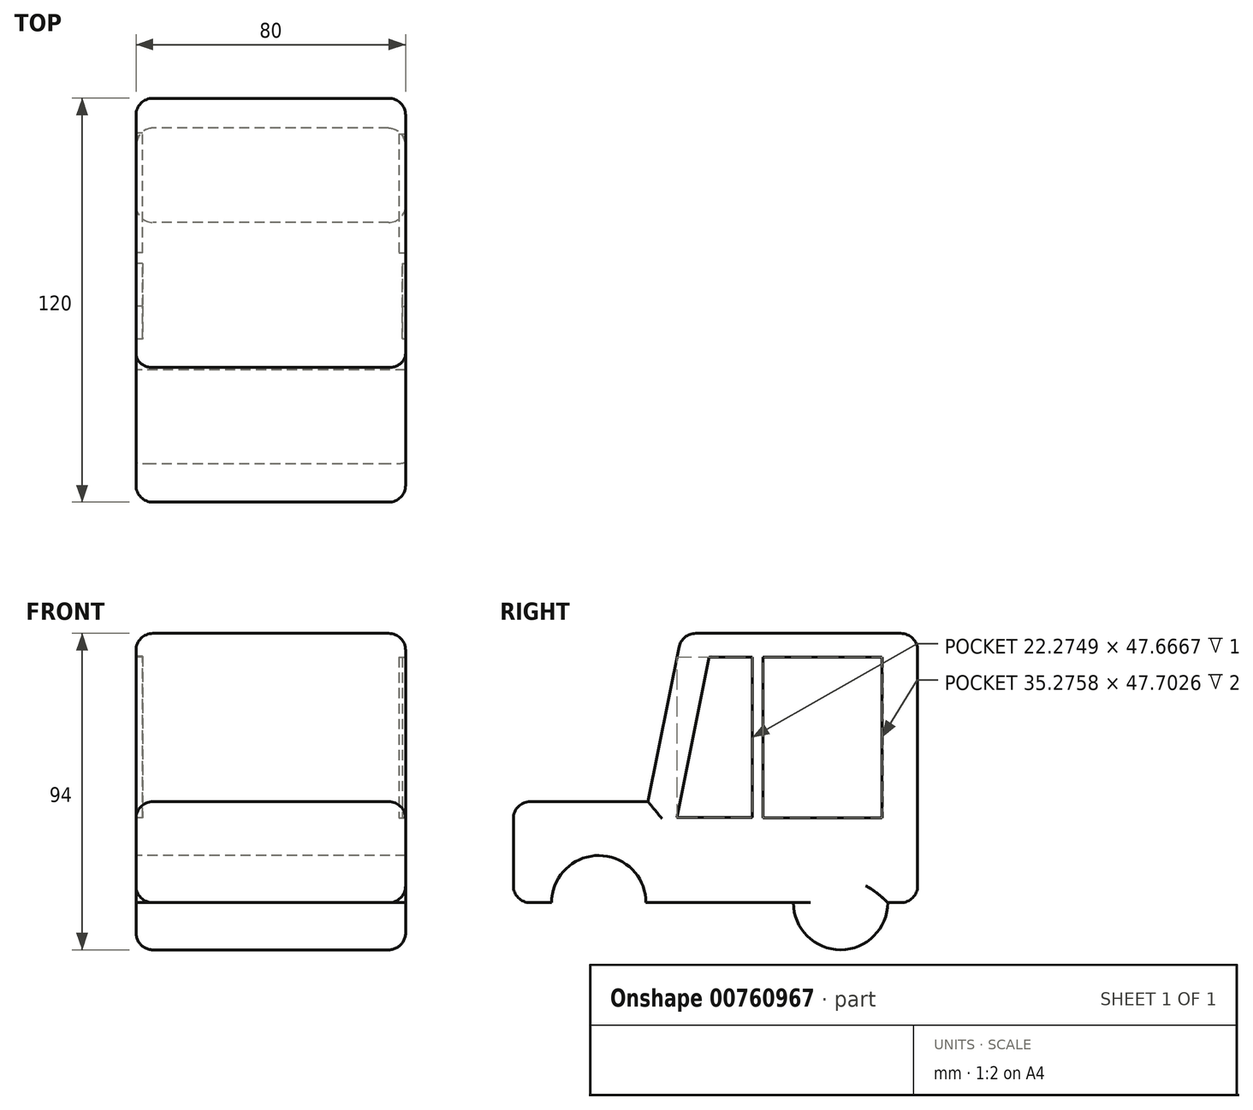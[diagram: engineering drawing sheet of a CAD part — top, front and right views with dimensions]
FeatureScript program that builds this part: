
annotation { "Feature Type Name" : "Feature", "Feature Type Description" : "" }
export const myFeature = defineFeature(function(context is Context, id is Id, definition is map)
    precondition{}
    {
        {
            var Q0;
            Q0=qCreatedBy(makeId("Right.planeOp"),FACE);
            var sketch = newSketch(context, id + "F0", { "sketchPlane" : qUnion([Q0])});
            skLineSegment(sketch, "E0", {"start": v(61.85, 80) * mm, "end": v(-8.15, 80) * mm});
            skLineSegment(sketch, "E1", {"start": v(-8.15, 80) * mm, "end": v(-18.15, 30) * mm});
            skLineSegment(sketch, "E2", {"start": v(-18.15, 30) * mm, "end": v(-58.15, 30) * mm});
            skLineSegment(sketch, "E3", {"start": v(-58.15, 30) * mm, "end": v(-58.15, 0) * mm});
            skLineSegment(sketch, "E4", {"start": v(-58.15, 0) * mm, "end": v(61.85, 0) * mm});
            skLineSegment(sketch, "E5", {"start": v(61.85, 0) * mm, "end": v(61.85, 80) * mm});
            skCircle(sketch, "E6", {"center": v(-32.81, 0) * mm, "radius": 14 * mm});
            skCircle(sketch, "E7", {"center": v(38.99, 0) * mm, "radius": 14 * mm});
            skSolve(sketch);
        }
        {
            var Q0;
            Q0=makeQuery(id+"F0.imprint","IMPRINT",FACE,{"disambiguationData":[TD([[makeQuery(id+"F0.imprint","IMPRINT",EDGE,{"derivedFrom":sQuery(id+"F0.wireOp",EDGE,"E0")}),1.0]])]});
            var sketch = newSketch(context, id + "F1", { "sketchPlane" : qUnion([Q0])});
            skSolve(sketch);
        }
        {
            var Q0;
            Q0 = qSketchRegion(id + "F1", true);
            var Q1;
            Q1=makeQuery(id+"F0.imprint","IMPRINT",FACE,{"disambiguationData":[TD([[makeQuery(id+"F0.imprint","IMPRINT",EDGE,{"derivedFrom":sQuery(id+"F0.wireOp",EDGE,"E0")}),1.0]])]});
            extrude(context, id + "F2", {"entities" : qUnion([Q0, Q1]), "depth" : 80 * mm, "offsetDistance" : 25 * mm});
        }
        {
            var Q0;
            {var subQ0=sQuery(id+"F0.wireOp",EDGE,"E6");var subQ1=sQuery(id+"F0.wireOp",EDGE,"E4");var subQ2=makeQuery(id+"F0.imprint","INTERSECT",VERTEX,{"disambiguationData":[OD(0.0)],"derivedFrom":[subQ1,subQ0]});Q0=makeQuery(id+"F0.imprint","IMPRINT",FACE,{"disambiguationData":[TD([[makeQuery(id+"F0.imprint","IMPRINT",EDGE,{"disambiguationData":[TD([[subQ2,-1.0]])],"derivedFrom":subQ1}),-1.0]])]});}
            var Q1;
            {var subQ0=sQuery(id+"F0.wireOp",EDGE,"E6");var subQ1=sQuery(id+"F0.wireOp",EDGE,"E4");var subQ2=makeQuery(id+"F0.imprint","INTERSECT",VERTEX,{"disambiguationData":[OD(0.0)],"derivedFrom":[subQ1,subQ0]});Q1=makeQuery(id+"F0.imprint","IMPRINT",FACE,{"disambiguationData":[TD([[makeQuery(id+"F0.imprint","IMPRINT",EDGE,{"disambiguationData":[TD([[subQ2,-1.0]])],"derivedFrom":subQ1}),1.0]])]});}
            extrude(context, id + "F3", {"entities" : qUnion([Q0, Q1]), "operationType" : NewBodyOperationType.ADD, "depth" : 80 * mm, "offsetDistance" : 25 * mm});
        }
        {
            var Q0;
            {var subQ0=sQuery(id+"F0.wireOp",EDGE,"E7");var subQ1=sQuery(id+"F0.wireOp",EDGE,"E4");var subQ2=makeQuery(id+"F0.imprint","INTERSECT",VERTEX,{"disambiguationData":[OD(0.0)],"derivedFrom":[subQ1,subQ0]});Q0=makeQuery(id+"F0.imprint","IMPRINT",FACE,{"disambiguationData":[TD([[makeQuery(id+"F0.imprint","IMPRINT",EDGE,{"disambiguationData":[TD([[subQ2,-1.0]])],"derivedFrom":subQ1}),1.0]])]});}
            var Q1;
            {var subQ0=sQuery(id+"F0.wireOp",EDGE,"E7");var subQ1=sQuery(id+"F0.wireOp",EDGE,"E4");var subQ2=makeQuery(id+"F0.imprint","INTERSECT",VERTEX,{"disambiguationData":[OD(0.0)],"derivedFrom":[subQ1,subQ0]});Q1=makeQuery(id+"F0.imprint","IMPRINT",FACE,{"disambiguationData":[TD([[makeQuery(id+"F0.imprint","IMPRINT",EDGE,{"disambiguationData":[TD([[subQ2,-1.0]])],"derivedFrom":subQ1}),-1.0]])]});}
            extrude(context, id + "F4", {"entities" : qUnion([Q0, Q1]), "operationType" : NewBodyOperationType.ADD, "depth" : 80 * mm, "offsetDistance" : 25 * mm});
        }
        {
            var Q0;
            Q0=makeQuery(id+"F2.opExtrude","CAP_EDGE",EDGE,{"disambiguationData":[OSD([sQuery(id+"F0.wireOp",EDGE,"E1")])],"isStart":false});
            var Q1;
            Q1=makeQuery(id+"F2.opExtrude","CAP_EDGE",EDGE,{"disambiguationData":[OSD([sQuery(id+"F0.wireOp",EDGE,"E0")])],"isStart":false});
            var Q2;
            Q2=makeQuery(id+"F2.opExtrude","SWEPT_EDGE",EDGE,{"disambiguationData":[OSD([sQuery(id+"F0.wireOp",EDGE,"E0"),sQuery(id+"F0.wireOp",EDGE,"E1")])]});
            var Q3;
            Q3=makeQuery(id+"F2.opExtrude","CAP_EDGE",EDGE,{"disambiguationData":[OSD([sQuery(id+"F0.wireOp",EDGE,"E2")])],"isStart":false});
            var Q4;
            Q4=makeQuery(id+"F2.opExtrude","SWEPT_EDGE",EDGE,{"disambiguationData":[OSD([sQuery(id+"F0.wireOp",EDGE,"E2"),sQuery(id+"F0.wireOp",EDGE,"E3")])]});
            var Q5;
            Q5=makeQuery(id+"F2.opExtrude","CAP_EDGE",EDGE,{"disambiguationData":[OSD([sQuery(id+"F0.wireOp",EDGE,"E3")])],"isStart":false});
            var Q6;
            Q6=makeQuery(id+"F2.opExtrude","CAP_EDGE",EDGE,{"disambiguationData":[OSD([sQuery(id+"F0.wireOp",EDGE,"E3")])],"isStart":true});
            var Q7;
            Q7=makeQuery(id+"F2.opExtrude","SWEPT_EDGE",EDGE,{"disambiguationData":[OSD([sQuery(id+"F0.wireOp",EDGE,"E3"),sQuery(id+"F0.wireOp",EDGE,"E4")])]});
            var Q8;
            Q8=makeQuery(id+"F3.opExtrude","CAP_EDGE",EDGE,{"disambiguationData":[OSD([sQuery(id+"F0.wireOp",EDGE,"E6")])],"isStart":true});
            var Q9;
            Q9=makeQuery(id+"F3.opExtrude","CAP_EDGE",EDGE,{"disambiguationData":[OSD([sQuery(id+"F0.wireOp",EDGE,"E6")])],"isStart":false});
            var Q10;
            Q10=makeQuery(id+"F4.opExtrude","CAP_EDGE",EDGE,{"disambiguationData":[OSD([sQuery(id+"F0.wireOp",EDGE,"E7")])],"isStart":false});
            var Q11;
            Q11=makeQuery(id+"F4.opExtrude","CAP_EDGE",EDGE,{"disambiguationData":[OSD([sQuery(id+"F0.wireOp",EDGE,"E7")])],"isStart":true});
            var Q12;
            Q12=makeQuery(id+"F2.opExtrude","CAP_EDGE",EDGE,{"disambiguationData":[OSD([sQuery(id+"F0.wireOp",EDGE,"E5")])],"isStart":false});
            var Q13;
            Q13=makeQuery(id+"F2.opExtrude","CAP_EDGE",EDGE,{"disambiguationData":[OSD([sQuery(id+"F0.wireOp",EDGE,"E5")])],"isStart":true});
            var Q14;
            Q14=makeQuery(id+"F2.opExtrude","CAP_EDGE",EDGE,{"disambiguationData":[OSD([sQuery(id+"F0.wireOp",EDGE,"E0")])],"isStart":true});
            var Q15;
            Q15=makeQuery(id+"F2.opExtrude","SWEPT_EDGE",EDGE,{"disambiguationData":[OSD([sQuery(id+"F0.wireOp",EDGE,"E0"),sQuery(id+"F0.wireOp",EDGE,"E5")])]});
            var Q16;
            {var subQ0=sQuery(id+"F0.wireOp",EDGE,"E4");Q16=makeQuery(id+"F2.opExtrude","CAP_EDGE",EDGE,{"disambiguationData":[OSD([subQ0]),TDD([makeQuery(id+"F0.imprint","IMPRINT",EDGE,{"disambiguationData":[TD([[makeQuery(id+"F0.imprint","INTERSECT",VERTEX,{"disambiguationData":[OD(1.0)],"derivedFrom":[subQ0,sQuery(id+"F0.wireOp",EDGE,"E6")]}),-1.0]])],"derivedFrom":subQ0})])],"isStart":true});}
            var Q17;
            {var subQ0=sQuery(id+"F0.wireOp",EDGE,"E4");Q17=makeQuery(id+"F2.opExtrude","CAP_EDGE",EDGE,{"disambiguationData":[OSD([subQ0]),TDD([makeQuery(id+"F0.imprint","IMPRINT",EDGE,{"disambiguationData":[TD([[makeQuery(id+"F0.imprint","INTERSECT",VERTEX,{"disambiguationData":[OD(1.0)],"derivedFrom":[subQ0,sQuery(id+"F0.wireOp",EDGE,"E6")]}),-1.0]])],"derivedFrom":subQ0})])],"isStart":false});}
            fillet(context, id + "F5", {"entities" : qUnion([Q0, Q1, Q2, Q3, Q4, Q5, Q6, Q7, Q8, Q9, Q10, Q11, Q12, Q13, Q14, Q15, Q16, Q17]), "radius" : 5 * mm, "tangentPropagation" : true, "allowEdgeOverflow" : false});
        }
        {
            var Q0;
            Q0=makeQuery(id+"F2.opExtrude","CAP_EDGE",EDGE,{"disambiguationData":[OSD([sQuery(id+"F0.wireOp",EDGE,"E2")])],"isStart":true});
            fillet(context, id + "F6", {"entities" : qUnion([Q0]), "radius" : 5 * mm, "tangentPropagation" : true, "allowEdgeOverflow" : false});
        }
        {
            var Q0;
            {var subQ0=sQuery(id+"F0.wireOp",EDGE,"E4");Q0=makeQuery(id+"F2.opExtrude","CAP_EDGE",EDGE,{"disambiguationData":[OSD([subQ0]),TDD([makeQuery(id+"F0.imprint","IMPRINT",EDGE,{"disambiguationData":[TD([[makeQuery(id+"F0.imprint","INTERSECT",VERTEX,{"derivedFrom":[sQuery(id+"F0.wireOp",EDGE,"E3"),subQ0]}),-1.0]])],"derivedFrom":subQ0})])],"isStart":false});}
            var Q1;
            {var subQ0=sQuery(id+"F0.wireOp",EDGE,"E4");Q1=makeQuery(id+"F2.opExtrude","CAP_EDGE",EDGE,{"disambiguationData":[OSD([subQ0]),TDD([makeQuery(id+"F0.imprint","IMPRINT",EDGE,{"disambiguationData":[TD([[makeQuery(id+"F0.imprint","INTERSECT",VERTEX,{"derivedFrom":[sQuery(id+"F0.wireOp",EDGE,"E3"),subQ0]}),-1.0]])],"derivedFrom":subQ0})])],"isStart":true});}
            fillet(context, id + "F7", {"entities" : qUnion([Q0, Q1]), "radius" : 5 * mm, "tangentPropagation" : true, "allowEdgeOverflow" : false});
        }
        {
            var Q0;
            {var subQ0=sQuery(id+"F0.wireOp",EDGE,"E7");var subQ1=sQuery(id+"F0.wireOp",EDGE,"E6");Q0=makeQuery(id+"F4.boolean.opBoolean","MERGE",FACE,{"derivedFrom":[makeQuery(id+"F3.boolean.opBoolean","MERGE",FACE,{"derivedFrom":[makeQuery(id+"F2.opExtrude","CAP_FACE",FACE,{"disambiguationData":[OSD([sQuery(id+"F0.wireOp",EDGE,"E0"),sQuery(id+"F0.wireOp",EDGE,"E1"),sQuery(id+"F0.wireOp",EDGE,"E2"),sQuery(id+"F0.wireOp",EDGE,"E3"),sQuery(id+"F0.wireOp",EDGE,"E4"),sQuery(id+"F0.wireOp",EDGE,"E5"),subQ1,subQ0])],"isStart":false}),makeQuery(id+"F3.opExtrude","CAP_FACE",FACE,{"disambiguationData":[OSD([subQ1])],"isStart":false})]}),makeQuery(id+"F4.opExtrude","CAP_FACE",FACE,{"disambiguationData":[OSD([subQ0])],"isStart":false})]});}
            var sketch = newSketch(context, id + "F8", { "sketchPlane" : qUnion([Q0])});
            skLineSegment(sketch, "E8", {"start": v(0, 72.95) * mm, "end": v(-9.53, 25.28) * mm});
            skLineSegment(sketch, "E9", {"start": v(-9.53, 25.28) * mm, "end": v(12.74, 25.28) * mm});
            skLineSegment(sketch, "E10", {"start": v(12.74, 25.28) * mm, "end": v(12.74, 72.95) * mm});
            skLineSegment(sketch, "E11", {"start": v(12.74, 72.95) * mm, "end": v(0, 72.95) * mm});
            skSolve(sketch);
        }
        {
            var Q0;
            Q0 = qSketchRegion(id + "F8", true);
            extrude(context, id + "F9", {"entities" : qUnion([Q0]), "operationType" : NewBodyOperationType.REMOVE, "endBound" : BoundingType.SYMMETRIC, "oppositeDirection" : true, "depth" : 2 * mm, "offsetDistance" : 25 * mm});
        }
        {
            var Q0;
            Q0=makeQuery(id+"F0.imprint","IMPRINT",FACE,{"disambiguationData":[TD([[makeQuery(id+"F0.imprint","IMPRINT",EDGE,{"derivedFrom":sQuery(id+"F0.wireOp",EDGE,"E0")}),1.0]])]});
            var sketch = newSketch(context, id + "F10", { "sketchPlane" : qUnion([Q0])});
            skLineSegment(sketch, "E12", {"start": v(0, 73.15) * mm, "end": v(-9.72, 25.25) * mm});
            skLineSegment(sketch, "E13", {"start": v(-9.72, 25.25) * mm, "end": v(12.73, 25.25) * mm});
            skLineSegment(sketch, "E14", {"start": v(12.73, 25.25) * mm, "end": v(12.73, 72.95) * mm});
            skLineSegment(sketch, "E15", {"start": v(12.73, 72.95) * mm, "end": v(0, 73.15) * mm});
            skSolve(sketch);
        }
        {
            var Q0;
            Q0 = qSketchRegion(id + "F10", true);
            extrude(context, id + "F11", {"entities" : qUnion([Q0]), "operationType" : NewBodyOperationType.REMOVE, "depth" : 2 * mm, "offsetDistance" : 25 * mm});
        }
        {
            var Q0;
            Q0=makeQuery(id+"F2.opExtrude","CAP_EDGE",EDGE,{"disambiguationData":[OSD([sQuery(id+"F0.wireOp",EDGE,"E1")])],"isStart":true});
            fillet(context, id + "F12", {"entities" : qUnion([Q0]), "radius" : 5 * mm, "tangentPropagation" : true, "allowEdgeOverflow" : false});
        }
        {
            var Q0;
            Q0=makeQuery(id+"F0.imprint","IMPRINT",FACE,{"disambiguationData":[TD([[makeQuery(id+"F0.imprint","IMPRINT",EDGE,{"derivedFrom":sQuery(id+"F0.wireOp",EDGE,"E0")}),1.0]])]});
            var sketch = newSketch(context, id + "F13", { "sketchPlane" : qUnion([Q0])});
            skLineSegment(sketch, "E16", {"start": v(15.93, 72.95) * mm, "end": v(51.51, 72.95) * mm});
            skLineSegment(sketch, "E17", {"start": v(51.51, 72.95) * mm, "end": v(51.51, 25.25) * mm});
            skLineSegment(sketch, "E18", {"start": v(51.51, 25.25) * mm, "end": v(15.93, 25.25) * mm});
            skLineSegment(sketch, "E19", {"start": v(15.93, 25.25) * mm, "end": v(15.93, 72.95) * mm});
            skSolve(sketch);
        }
        {
            var Q0;
            Q0 = qSketchRegion(id + "F13", true);
            extrude(context, id + "F14", {"entities" : qUnion([Q0]), "operationType" : NewBodyOperationType.REMOVE, "depth" : 2 * mm, "offsetDistance" : 25 * mm});
        }
        {
            var Q0;
            {var subQ0=sQuery(id+"F0.wireOp",EDGE,"E7");var subQ1=sQuery(id+"F0.wireOp",EDGE,"E6");Q0=makeQuery(id+"F4.boolean.opBoolean","MERGE",FACE,{"derivedFrom":[makeQuery(id+"F3.boolean.opBoolean","MERGE",FACE,{"derivedFrom":[makeQuery(id+"F2.opExtrude","CAP_FACE",FACE,{"disambiguationData":[OSD([sQuery(id+"F0.wireOp",EDGE,"E0"),sQuery(id+"F0.wireOp",EDGE,"E1"),sQuery(id+"F0.wireOp",EDGE,"E2"),sQuery(id+"F0.wireOp",EDGE,"E3"),sQuery(id+"F0.wireOp",EDGE,"E4"),sQuery(id+"F0.wireOp",EDGE,"E5"),subQ1,subQ0])],"isStart":false}),makeQuery(id+"F3.opExtrude","CAP_FACE",FACE,{"disambiguationData":[OSD([subQ1])],"isStart":false})]}),makeQuery(id+"F4.opExtrude","CAP_FACE",FACE,{"disambiguationData":[OSD([subQ0])],"isStart":false})]});}
            var sketch = newSketch(context, id + "F15", { "sketchPlane" : qUnion([Q0])});
            skLineSegment(sketch, "E20", {"start": v(15.93, 72.95) * mm, "end": v(15.93, 25.25) * mm});
            skLineSegment(sketch, "E21", {"start": v(15.93, 25.25) * mm, "end": v(51.21, 25.25) * mm});
            skLineSegment(sketch, "E22", {"start": v(51.21, 25.25) * mm, "end": v(51.21, 72.95) * mm});
            skLineSegment(sketch, "E23", {"start": v(51.21, 72.95) * mm, "end": v(15.93, 72.95) * mm});
            skSolve(sketch);
        }
        {
            var Q0;
            Q0 = qSketchRegion(id + "F15", true);
            extrude(context, id + "F16", {"entities" : qUnion([Q0]), "operationType" : NewBodyOperationType.REMOVE, "oppositeDirection" : true, "depth" : 2 * mm, "offsetDistance" : 25 * mm});
        }
        {
            var Q0;
            Q0=makeQuery(id+"F2.opExtrude","SWEPT_EDGE",EDGE,{"disambiguationData":[OSD([sQuery(id+"F0.wireOp",EDGE,"E4"),sQuery(id+"F0.wireOp",EDGE,"E5")])]});
            fillet(context, id + "F17", {"entities" : qUnion([Q0]), "radius" : 5 * mm, "tangentPropagation" : true, "allowEdgeOverflow" : false});
        }
    });
